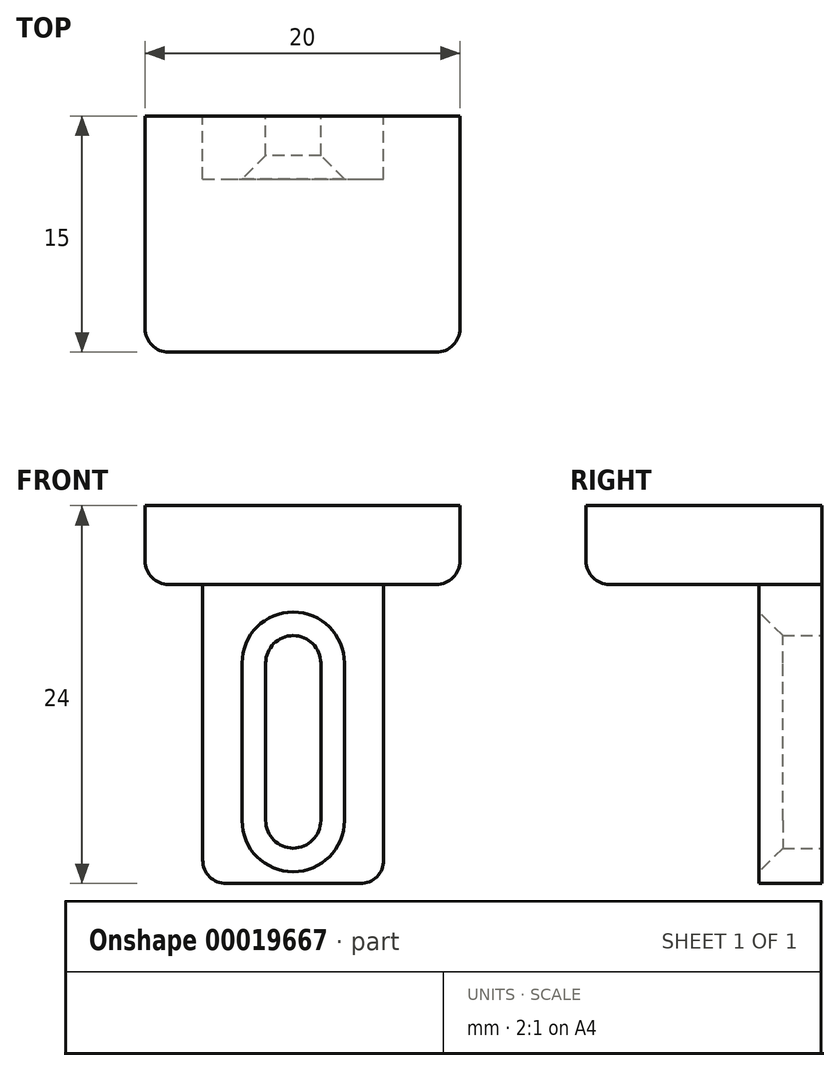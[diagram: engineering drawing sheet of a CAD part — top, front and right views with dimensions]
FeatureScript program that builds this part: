
annotation { "Feature Type Name" : "Feature", "Feature Type Description" : "" }
export const myFeature = defineFeature(function(context is Context, id is Id, definition is map)
    precondition{}
    {
        {
            var Q0;
            Q0=qCreatedBy(makeId("Front.planeOp"),FACE);
            var sketch = newSketch(context, id + "F0", { "sketchPlane" : qUnion([Q0])});
            skLineSegment(sketch, "E0.left", {"start": v(20.7, 42.3) * mm, "end": v(20.7, 32.3) * mm});
            skLineSegment(sketch, "E0.right", {"start": v(24.2, 42.3) * mm, "end": v(24.2, 32.3) * mm});
            skArc(sketch, "E1", {"start": v(24.2, 42.3) * mm, "mid": v(22.45, 44.05) * mm, "end": v(20.7, 42.3) * mm});
            skArc(sketch, "E2", {"start": v(20.7, 32.3) * mm, "mid": v(22.45, 30.55) * mm, "end": v(24.2, 32.3) * mm});
            skLineSegment(sketch, "E3.bottom", {"start": v(16.7, 52.3) * mm, "end": v(28.2, 52.3) * mm});
            skLineSegment(sketch, "E3.top", {"start": v(16.7, 28.3) * mm, "end": v(28.2, 28.3) * mm});
            skLineSegment(sketch, "E3.left", {"start": v(16.7, 52.3) * mm, "end": v(16.7, 28.3) * mm});
            skLineSegment(sketch, "E3.right", {"start": v(28.2, 52.3) * mm, "end": v(28.2, 28.3) * mm});
            skLineSegment(sketch, "E4", {"start": v(22.45, 56.12) * mm, "end": v(22.45, 19.51) * mm, "construction": true});
            skPoint(sketch, "E5", {"position": v(22.45, 28.3) * mm});
            skLineSegment(sketch, "E6.bottom", {"start": v(13.04, 52.3) * mm, "end": v(33.04, 52.3) * mm});
            skLineSegment(sketch, "E6.top", {"start": v(13.04, 47.3) * mm, "end": v(33.04, 47.3) * mm});
            skLineSegment(sketch, "E6.left", {"start": v(13.04, 52.3) * mm, "end": v(13.04, 47.3) * mm});
            skLineSegment(sketch, "E6.right", {"start": v(33.04, 52.3) * mm, "end": v(33.04, 47.3) * mm});
            skSolve(sketch);
        }
        {
            var Q0;
            Q0=makeQuery(id+"F0.imprint","IMPRINT",FACE,{"disambiguationData":[TD([[makeQuery(id+"F0.imprint","IMPRINT",EDGE,{"derivedFrom":sQuery(id+"F0.wireOp",EDGE,"E0.left")}),-1.0]])]});
            extrude(context, id + "F1", {"entities" : qUnion([Q0]), "depth" : 4 * mm});
        }
        {
            var Q0;
            {var subQ0=sQuery(id+"F0.wireOp",EDGE,"E6.right");Q0=makeQuery(id+"F0.imprint","IMPRINT",FACE,{"disambiguationData":[TD([[makeQuery(id+"F0.imprint","IMPRINT",EDGE,{"derivedFrom":subQ0}),-1.0]])]});}
            var Q1;
            {var subQ3=sQuery(id+"F0.wireOp",EDGE,"E3.left");var subQ5=sQuery(id+"F0.wireOp",EDGE,"E6.bottom");var subQ7=makeQuery(id+"F0.imprint","INTERSECT",VERTEX,{"derivedFrom":[subQ3,subQ5]});Q1=makeQuery(id+"F0.imprint","IMPRINT",FACE,{"disambiguationData":[TD([[makeQuery(id+"F0.imprint","IMPRINT",EDGE,{"disambiguationData":[TD([[subQ7,-1.0]])],"derivedFrom":subQ3}),1.0]])]});}
            var Q2;
            {var subQ0=sQuery(id+"F0.wireOp",EDGE,"E6.left");Q2=makeQuery(id+"F0.imprint","IMPRINT",FACE,{"disambiguationData":[TD([[makeQuery(id+"F0.imprint","IMPRINT",EDGE,{"derivedFrom":subQ0}),1.0]])]});}
            extrude(context, id + "F2", {"entities" : qUnion([Q0, Q1, Q2]), "operationType" : NewBodyOperationType.ADD, "depth" : 15 * mm});
        }
        {
            var Q0;
            Q0=makeQuery(id+"F1.opExtrude","CAP_EDGE",EDGE,{"disambiguationData":[OSD([sQuery(id+"F0.wireOp",EDGE,"E0.left")])],"isStart":false});
            chamfer(context, id + "F3", {"entities" : qUnion([Q0]), "width" : 1.5 * mm, "tangentPropagation" : true});
        }
        {
            var Q0;
            Q0=makeQuery(id+"F2.opExtrude","SWEPT_EDGE",EDGE,{"disambiguationData":[OSD([sQuery(id+"F0.wireOp",EDGE,"E6.top"),sQuery(id+"F0.wireOp",EDGE,"E6.right")])]});
            var Q1;
            Q1=makeQuery(id+"F1.opExtrude","SWEPT_EDGE",EDGE,{"disambiguationData":[OSD([sQuery(id+"F0.wireOp",EDGE,"E3.top"),sQuery(id+"F0.wireOp",EDGE,"E3.left")])]});
            var Q2;
            Q2=makeQuery(id+"F1.opExtrude","SWEPT_EDGE",EDGE,{"disambiguationData":[OSD([sQuery(id+"F0.wireOp",EDGE,"E3.top"),sQuery(id+"F0.wireOp",EDGE,"E3.right")])]});
            var Q3;
            Q3=makeQuery(id+"F2.opExtrude","CAP_EDGE",EDGE,{"disambiguationData":[OSD([sQuery(id+"F0.wireOp",EDGE,"E6.right")])],"isStart":false});
            var Q4;
            Q4=makeQuery(id+"F2.opExtrude","CAP_EDGE",EDGE,{"disambiguationData":[OSD([sQuery(id+"F0.wireOp",EDGE,"E6.left")])],"isStart":false});
            var Q5;
            Q5=makeQuery(id+"F2.opExtrude","SWEPT_EDGE",EDGE,{"disambiguationData":[OSD([sQuery(id+"F0.wireOp",EDGE,"E6.top"),sQuery(id+"F0.wireOp",EDGE,"E6.left")])]});
            var Q6;
            Q6=makeQuery(id+"F2.opExtrude","CAP_EDGE",EDGE,{"disambiguationData":[OSD([sQuery(id+"F0.wireOp",EDGE,"E6.top")])],"isStart":false});
            fillet(context, id + "F4", {"entities" : qUnion([Q0, Q1, Q2, Q3, Q4, Q5, Q6]), "radius" : 1.5 * mm, "tangentPropagation" : true, "allowEdgeOverflow" : false});
        }
    });
